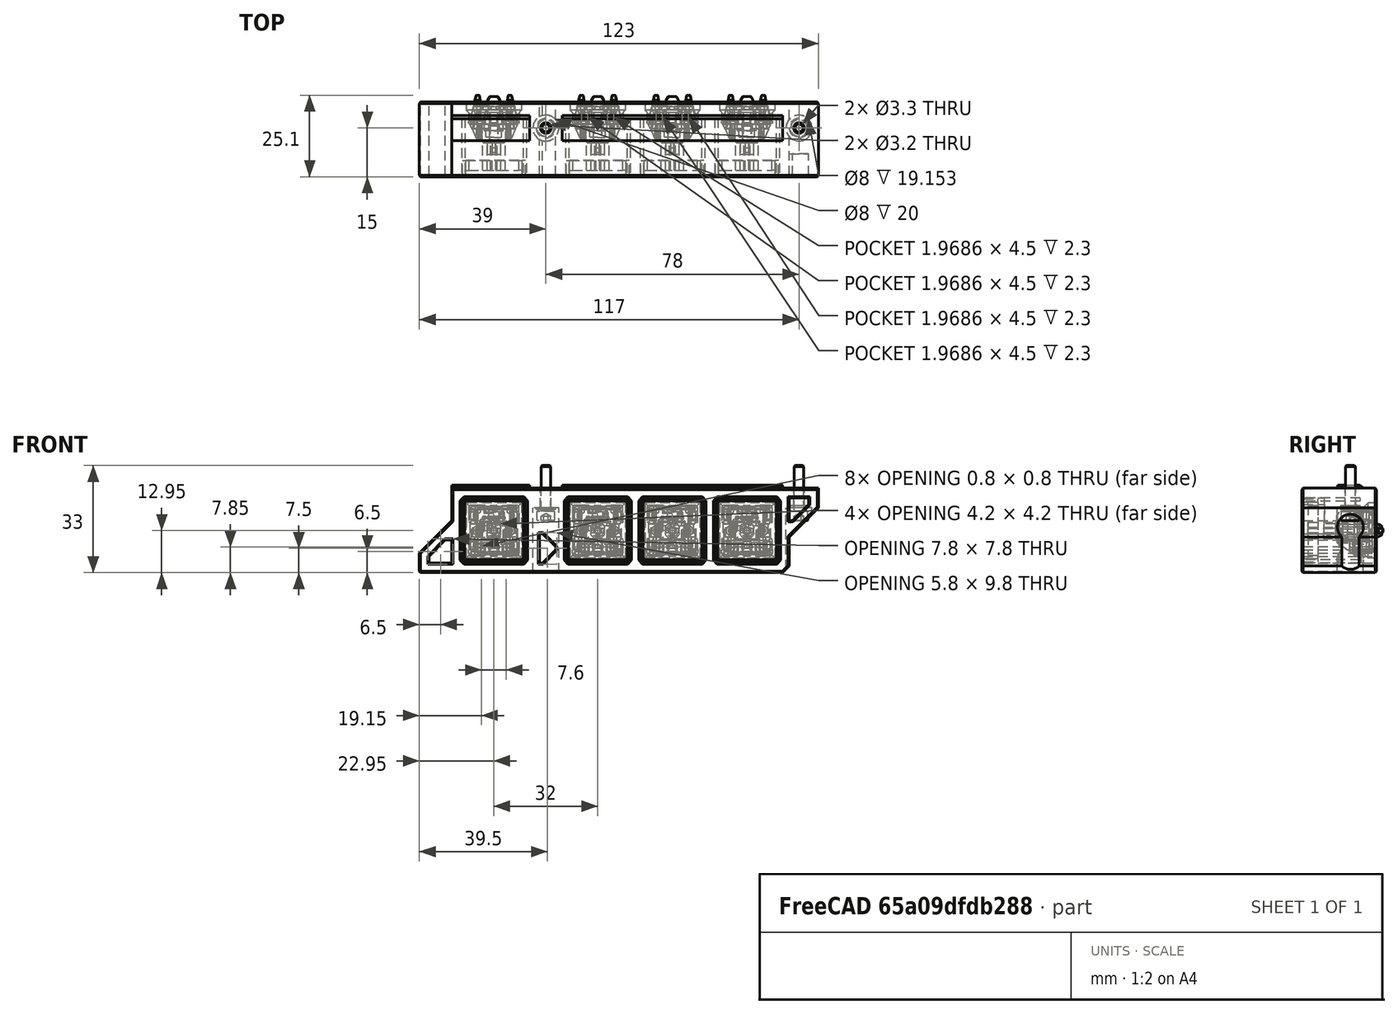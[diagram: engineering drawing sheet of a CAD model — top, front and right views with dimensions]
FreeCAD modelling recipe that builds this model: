
FCSTD DOCUMENT  (FreeCAD 0.19R24291 (Git))
Label: cherrymz-button-assembly
License: Other
LicenseURL: GPL3
objects: Part::Feature×9, Part::FeaturePython×4, PartDesign::CoordinateSystem×1, App::Part×1
note: 14 computed .brp shape members not serialized (recipe doc carries the construction recipe); baked Part::Feature solids carry a one-line shape summary decoded from their .brp

FEATURE [Part::Feature] Fusion001  label="cherrymx"
  Placement = pos=(30.3,16.2,20.3) rot=(0,0,1;3.14159rad)
  shape: bbox 15.74 x 18.31 x 15.74 mm, 1615 faces (baked)
FEATURE [Part::Feature] Fusion001002006001  label="button-cap"
  Placement = pos=(23,3e-15,13) rot=(-1,0,0;1.5708rad)
  shape: bbox 19.4 x 11 x 19.4 mm, 49 faces (baked)
FEATURE [Part::Feature] Fusion001002006002  label="cherrymx001"
  Placement = pos=(62.3,16.2,20.3) rot=(0,0,1;3.14159rad)
  shape: bbox 15.74 x 18.31 x 15.74 mm, 1615 faces (baked)
FEATURE [Part::Feature] Fusion001002006003  label="cherrymx002"
  Placement = pos=(85.3,16.2,20.3) rot=(0,0,1;3.14159rad)
  shape: bbox 15.74 x 18.31 x 15.74 mm, 1615 faces (baked)
FEATURE [Part::Feature] Fusion001002006004  label="cherrymx003"
  Placement = pos=(108.3,16.2,20.3) rot=(0,0,1;3.14159rad)
  shape: bbox 15.74 x 18.31 x 15.74 mm, 1615 faces (baked)
FEATURE [Part::Feature] Fusion001002006005  label="button-cap001"
  Placement = pos=(55,3e-15,13) rot=(-1,0,0;1.5708rad)
  shape: bbox 19.4 x 11 x 19.4 mm, 49 faces (baked)
FEATURE [Part::Feature] Fusion001002006006  label="button-cap002"
  Placement = pos=(78,3e-15,13) rot=(-1,0,0;1.5708rad)
  shape: bbox 19.4 x 11 x 19.4 mm, 49 faces (baked)
FEATURE [Part::Feature] Fusion001002006007  label="button-cap003"
  Placement = pos=(101,3e-15,13) rot=(-1,0,0;1.5708rad)
  shape: bbox 19.4 x 11 x 19.4 mm, 49 faces (baked)
FEATURE [PartDesign::CoordinateSystem] LCS_cherrymx_button  label="LCS_cherrymx-button"
  AttacherType = Attacher::AttachEngine3D
FEATURE [Part::FeaturePython] Screw  label="M3x14-Screw001"  # Fasteners workbench fastener (typed FeaturePython)
  Placement = pos=(39,15,19) rot=(1,0,0;3.14159rad)
  diameter = 4
  invert = true
  length = 5
  lengthCustom = 14
  matchOuter = true
  offset = 1
  thread = false
  type = 34
FEATURE [Part::FeaturePython] Screw001  label="M3x14-Screw"  # Fasteners workbench fastener (typed FeaturePython)
  Placement = pos=(117,15,19) rot=(1,0,0;3.14159rad)
  diameter = 4
  invert = true
  length = 5
  lengthCustom = 14
  matchOuter = true
  offset = 1
  thread = false
  type = 34
FEATURE [Part::FeaturePython] Washer  label="M3-Washer"  # Fasteners workbench fastener (typed FeaturePython)
  Placement = pos=(39,15,20) rot=(1,0,0;3.14159rad)
  diameter = 4
  invert = true
  matchOuter = true
  offset = 0
  type = 5
FEATURE [Part::FeaturePython] Washer001  label="M3-Washer001"  # Fasteners workbench fastener (typed FeaturePython)
  Placement = pos=(117,15,20) rot=(0,0,1;0rad)
  diameter = 4
  invert = false
  matchOuter = true
  offset = 0
  type = 5
FEATURE [Part::Feature] Cut008004003004014002002008004001001  label="cherrymx_mounter"
  shape: bbox 123 x 23 x 27 mm, 296 faces (baked)
FEATURE [App::Part] Part  label="cherrymx-button"
  Group = -> [Fusion001,Fusion001002006001,Fusion001002006002,Fusion001002006003,Fusion001002006004,Fusion001002006005,Fusion001002006006,Fusion001002006007,LCS_cherrymx_button,Screw001,Screw,Washer,Washer001,Cut008004003004014002002008004001001]
  Origin = -> Origin
